# Revit family: Konsolenset, schallgedämmt
name_source: partatom
category: HLS-Bauteile
revit_build: Autodesk Revit 2017 (Build: 20190507_1515(x64)
units: mm (PartAtom-declared; Revit-internal decimal feet)

## family parameters
Arbeitsebenenbasiert = Ja
Beim Laden mit Abzugskörper schneiden = Nein
Bemaßung runder Anschluss = Durchmesser verwenden
Gemeinsam genutzt = Ja
Immer vertikal = Nein
Raumberechnungspunkt = Nein
Teiletyp = Normal

## types (3) — shared parameters
Fabrikat = MEFA
Firma = MEFA Befestigungs- und Montagesysteme GmbH
Kurztext1 = Konsolenset Stex 35/42 schallg.
Material = Stahl
Material Dämmelement = Gummi SBR
Oberflaeche = galvanisch verzinkt
Profiltyp = Stex 35/42/1,5
Vorgabe-Ansicht = 1219 mm
max. Temperaturbeständigkeit = 100 °C

## per-type parameters (varying)
| type | Artikelnummer | D | EAN | Gewicht | Gewicht pro Bauteil | Kurztext2 | Länge | Mengeneinheit | d2 | max. zul. Last (gesamt) | max. zul. Last pro Kragarm | vpe |
| Konsolenset, schallgedämmt Set 1 L= 450 | 0813500450 | 500 mm  [stored 1.64042 ft] | 4250928419699 | 4.76 kg | 4.76 kg | Länge 450 mm | 450 mm  [stored 1.47638 ft] | SET | 250 mm  [stored 0.82021 ft] | 2,78 kN | 1,39 kN | 1 SET |
| Konsolenset, schallgedämmt Set 2 L= 525 | 0813500526 | 550 mm | 4250928419705 | 5.00 kg | 5.00 kg | Länge 525 mm | 525 mm | SET | 275 mm | 2,38 kN | 1,19 kN | 1 SET |
| Konsolenset, schallgedämmt Set 3 L= 600 | 0813500600 | 580 mm  [stored 1.90289 ft] | 4250928419712 | 5.25 kg | 5.25 kg | Länge 600 mm | 600 mm | St | 290 mm  [stored 0.951444 ft] | 2,08 kN | 1,04 kN | 1 St |

note: column(s) folded — value = type name in every type: Konsolenset

note: [stored X ft] marks values corroborated as IEEE doubles in the binary element streams (Revit-internal decimal feet)

## geometry (parser evidence)
native form markers: Sweep x5
no freeform markers — native parametric forms only
